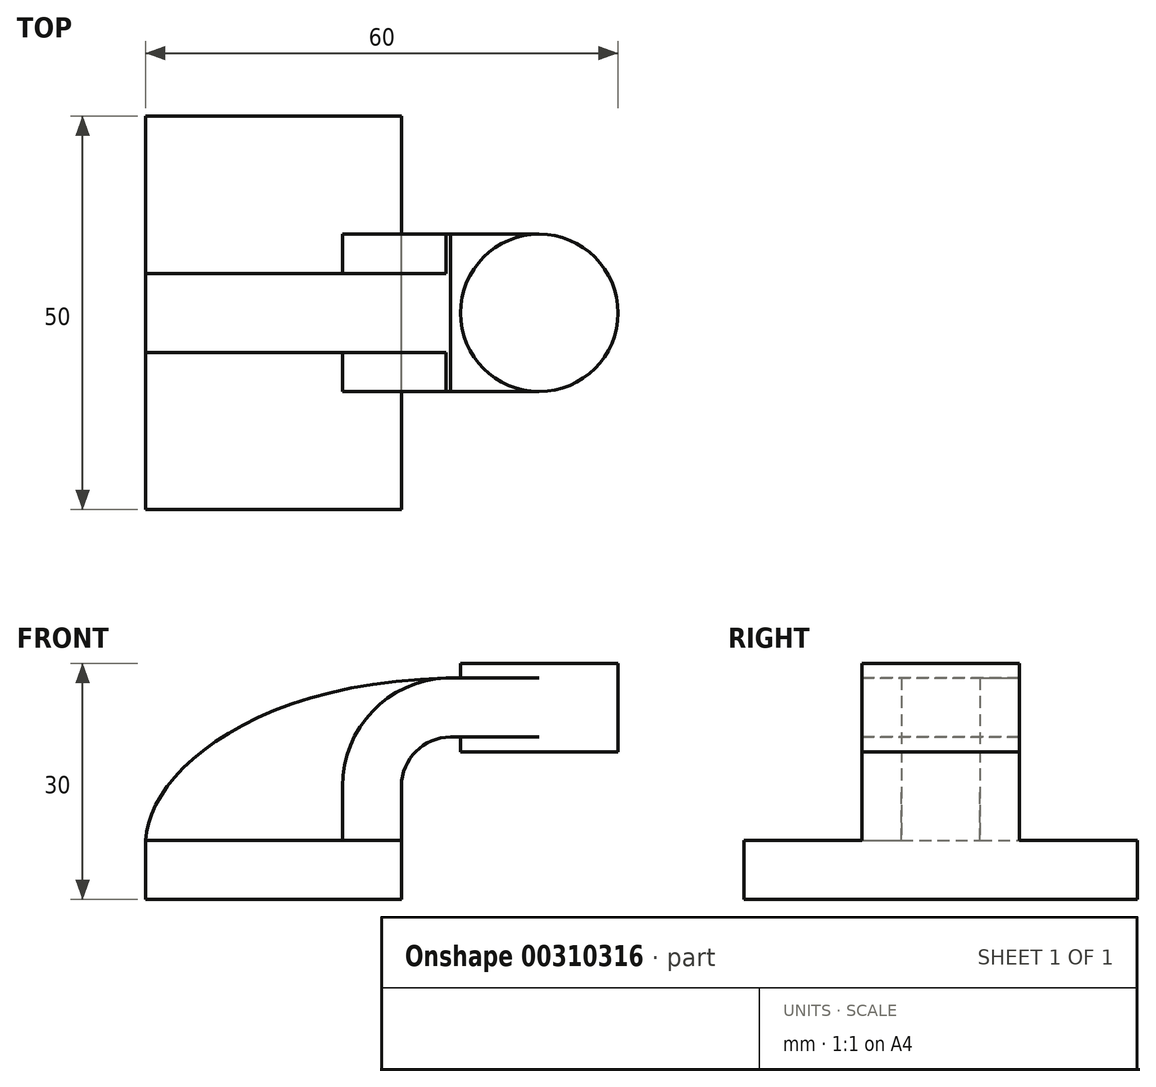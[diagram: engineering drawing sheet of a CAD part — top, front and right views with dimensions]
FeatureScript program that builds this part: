
annotation { "Feature Type Name" : "Feature", "Feature Type Description" : "" }
export const myFeature = defineFeature(function(context is Context, id is Id, definition is map)
    precondition{}
    {
        {
            var Q0;
            Q0=qCreatedBy(makeId("Front.planeOp"),FACE);
            var sketch = newSketch(context, id + "F0", { "sketchPlane" : qUnion([Q0])});
            skLineSegment(sketch, "E0.bottom", {"start": v(-16.25, -3.75) * mm, "end": v(16.25, -3.75) * mm});
            skLineSegment(sketch, "E0.top", {"start": v(-16.25, 3.75) * mm, "end": v(16.25, 3.75) * mm});
            skLineSegment(sketch, "E0.left", {"start": v(-16.25, -3.75) * mm, "end": v(-16.25, 3.75) * mm});
            skLineSegment(sketch, "E0.right", {"start": v(16.25, -3.75) * mm, "end": v(16.25, 3.75) * mm});
            skPoint(sketch, "E0.middle", {"position": v(0, 0) * mm});
            skLineSegment(sketch, "E1.bottom", {"start": v(23.75, 15) * mm, "end": v(43.75, 15) * mm});
            skLineSegment(sketch, "E1.top", {"start": v(23.75, 26.25) * mm, "end": v(43.75, 26.25) * mm});
            skLineSegment(sketch, "E1.left", {"start": v(23.75, 15) * mm, "end": v(23.75, 26.25) * mm});
            skLineSegment(sketch, "E1.right", {"start": v(43.75, 15) * mm, "end": v(43.75, 26.25) * mm});
            skPoint(sketch, "E1.middle", {"position": v(33.75, 20.62) * mm});
            skLineSegment(sketch, "E2", {"start": v(16.25, 3.75) * mm, "end": v(16.25, 10.63) * mm});
            skArc(sketch, "E3", {"start": v(16.25, 10.63) * mm, "mid": v(18.08, 15.05) * mm, "end": v(22.5, 16.88) * mm});
            skLineSegment(sketch, "E4", {"start": v(22.5, 16.88) * mm, "end": v(33.75, 16.88) * mm});
            skLineSegment(sketch, "E5.0", {"start": v(22.5, 24.38) * mm, "end": v(33.75, 24.38) * mm});
            skArc(sketch, "E5.1", {"start": v(8.75, 10.63) * mm, "mid": v(12.78, 20.35) * mm, "end": v(22.5, 24.38) * mm});
            skLineSegment(sketch, "E5.2", {"start": v(8.75, 3.75) * mm, "end": v(8.75, 10.63) * mm});
            skFitSpline(sketch, "E6", {"points": [v(22.5, 24.38) * mm, v(-16.25, 3.75) * mm], "startDerivative": vector(-77.2, -1.42) * mm, "endDerivative": vector(-0.94, -24.38) * mm});
            skLineSegment(sketch, "E7", {"start": v(33.75, 26.25) * mm, "end": v(33.75, 15) * mm});
            skSolve(sketch);
        }
        {
            var Q0;
            Q0=makeQuery(id+"F0.imprint","IMPRINT",FACE,{"disambiguationData":[TD([[makeQuery(id+"F0.imprint","IMPRINT",EDGE,{"derivedFrom":sQuery(id+"F0.wireOp",EDGE,"E0.bottom")}),1.0]])]});
            extrude(context, id + "F1", {"entities" : qUnion([Q0]), "endBound" : BoundingType.SYMMETRIC, "depth" : 50 * mm});
        }
        {
            var Q0;
            {var subQ3=sQuery(id+"F0.wireOp",EDGE,"E5.2");Q0=makeQuery(id+"F0.imprint","IMPRINT",FACE,{"disambiguationData":[TD([[makeQuery(id+"F0.imprint","IMPRINT",EDGE,{"derivedFrom":subQ3}),1.0]])]});}
            extrude(context, id + "F2", {"entities" : qUnion([Q0]), "operationType" : NewBodyOperationType.ADD, "endBound" : BoundingType.SYMMETRIC, "depth" : 10 * mm});
        }
        {
            var Q0;
            {var subQ1=sQuery(id+"F0.wireOp",EDGE,"E2");Q0=makeQuery(id+"F0.imprint","IMPRINT",FACE,{"disambiguationData":[TD([[makeQuery(id+"F0.imprint","IMPRINT",EDGE,{"derivedFrom":subQ1}),1.0]])]});}
            var Q1;
            {var subQ0=sQuery(id+"F0.wireOp",EDGE,"E4");var subQ1=sQuery(id+"F0.wireOp",EDGE,"E1.left");var subQ2=makeQuery(id+"F0.imprint","INTERSECT",VERTEX,{"derivedFrom":[subQ1,subQ0]});Q1=makeQuery(id+"F0.imprint","IMPRINT",FACE,{"disambiguationData":[TD([[makeQuery(id+"F0.imprint","IMPRINT",EDGE,{"disambiguationData":[TD([[subQ2,-1.0]])],"derivedFrom":subQ1}),-1.0]])]});}
            extrude(context, id + "F3", {"entities" : qUnion([Q0, Q1]), "operationType" : NewBodyOperationType.ADD, "endBound" : BoundingType.SYMMETRIC, "depth" : 20 * mm});
        }
        {
            var Q0;
            {var subQ4=sQuery(id+"F0.wireOp",EDGE,"E1.right");Q0=makeQuery(id+"F0.imprint","IMPRINT",FACE,{"disambiguationData":[TD([[makeQuery(id+"F0.imprint","IMPRINT",EDGE,{"derivedFrom":subQ4}),1.0]])]});}
            var Q1;
            Q1=sQuery(id+"F0.wireOp",EDGE,"E7");
            revolve(context, id + "F4", {"operationType" : NewBodyOperationType.ADD, "entities" : qUnion([Q0]), "axis" : qUnion([Q1]), "revolveType" : RevolveType.FULL});
        }
    });
